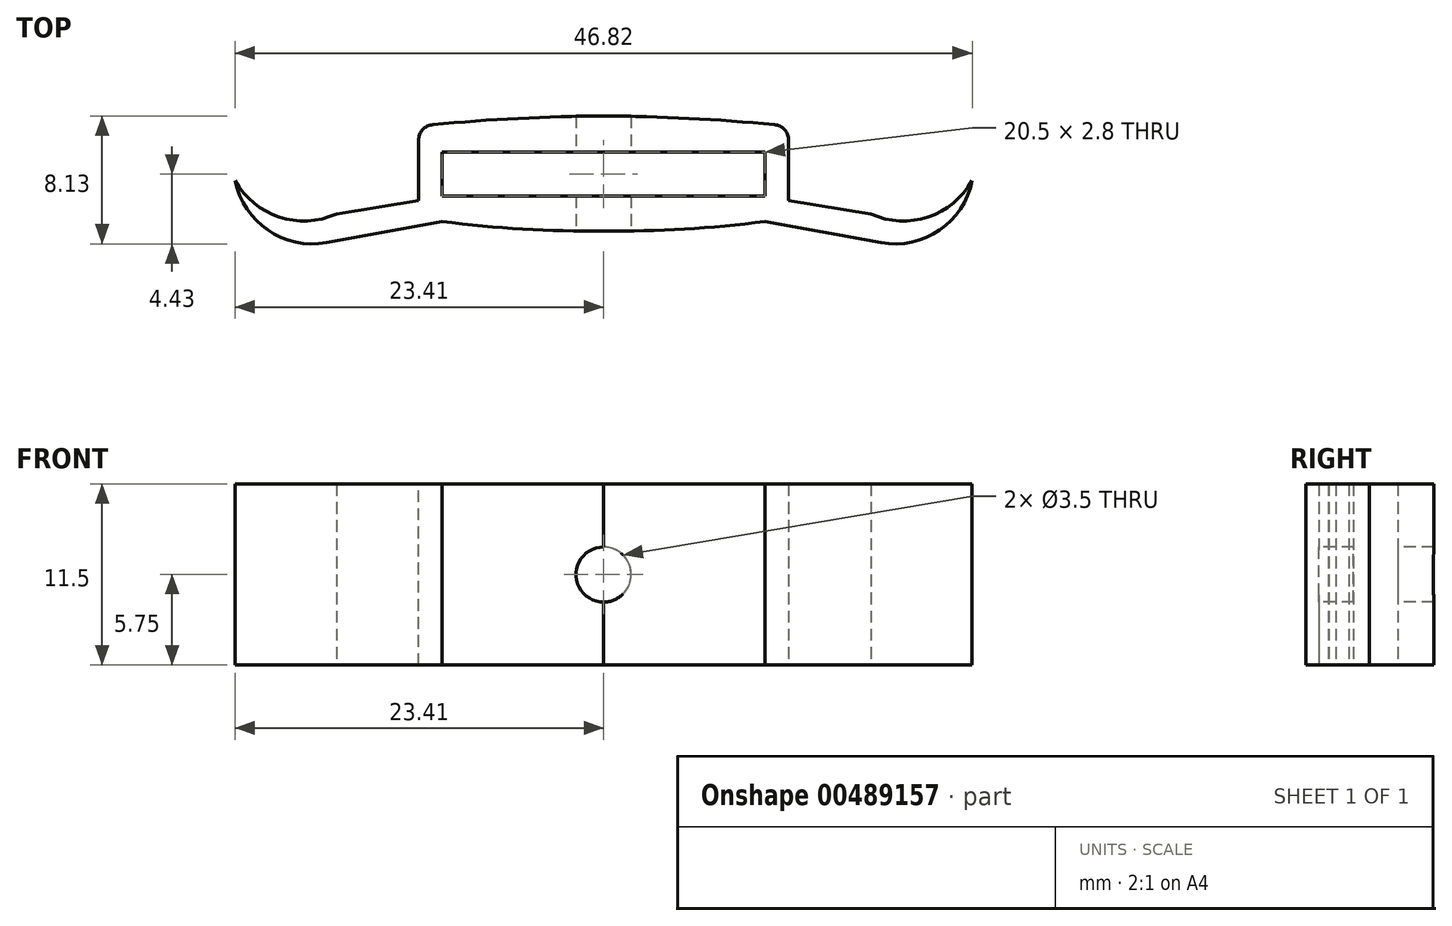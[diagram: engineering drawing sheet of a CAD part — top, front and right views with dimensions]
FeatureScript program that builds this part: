
annotation { "Feature Type Name" : "Feature", "Feature Type Description" : "" }
export const myFeature = defineFeature(function(context is Context, id is Id, definition is map)
    precondition{}
    {
        {
            var Q0;
            Q0=qCreatedBy(makeId("Top.planeOp"),FACE);
            var sketch = newSketch(context, id + "F0", { "sketchPlane" : qUnion([Q0])});
            skLineSegment(sketch, "E0", {"start": v(23.5, -4.04) * mm, "end": v(23.5, 3) * mm, "construction": true});
            skLineSegment(sketch, "E1", {"start": v(29.72, 8.1) * mm, "end": v(-41.61, 8.1) * mm, "construction": true});
            skLineSegment(sketch, "E2", {"start": v(30.67, 18.45) * mm, "end": v(-38.25, 18.45) * mm, "construction": true});
            skLineSegment(sketch, "E3", {"start": v(10.25, -6.45) * mm, "end": v(10.25, 31.2) * mm, "construction": true});
            skLineSegment(sketch, "E4", {"start": v(27.36, 1.4) * mm, "end": v(-25.89, 1.4) * mm, "construction": true});
            skLineSegment(sketch, "E5", {"start": v(10.25, 1.4) * mm, "end": v(17.87, 0) * mm});
            skArc(sketch, "E6", {"start": v(0, 0.8) * mm, "mid": v(5.14, 0.9) * mm, "end": v(10.25, 1.4) * mm});
            skArc(sketch, "E7", {"start": v(16.98, 1.87) * mm, "mid": v(20.6, 1.68) * mm, "end": v(23.4, 4) * mm});
            skLineSegment(sketch, "E8.trimOffspring", {"start": v(23.5, 8.1) * mm, "end": v(23.5, 14.66) * mm, "construction": true});
            skArc(sketch, "E9.trimOffspring", {"start": v(17.58, 0.05) * mm, "mid": v(21.3, 0.83) * mm, "end": v(23.4, 4) * mm});
            skPoint(sketch, "E10.center.orphan", {"position": v(19.03, 5.12) * mm});
            skLineSegment(sketch, "E11", {"start": v(10.25, 3) * mm, "end": v(10.25, 5.8) * mm});
            skLineSegment(sketch, "E12", {"start": v(10.25, 5.8) * mm, "end": v(0, 5.8) * mm});
            skLineSegment(sketch, "E13", {"start": v(10.25, 3) * mm, "end": v(0, 3) * mm});
            skLineSegment(sketch, "E14", {"start": v(11.75, 2.71) * mm, "end": v(11.75, 7.46) * mm});
            skArc(sketch, "E15", {"start": v(11.75, 7.46) * mm, "mid": v(5.88, 7.92) * mm, "end": v(0, 8.1) * mm});
            skLineSegment(sketch, "E16", {"start": v(23.4, 4) * mm, "end": v(23.4, 4) * mm});
            skLineSegment(sketch, "E17.MirrorCS", {"start": v(-11.75, 2.71) * mm, "end": v(-11.75, 7.46) * mm});
            skLineSegment(sketch, "E18.MirrorCS", {"start": v(-10.25, 3) * mm, "end": v(0, 3) * mm});
            skArc(sketch, "E19.MirrorCS", {"start": v(-11.75, 7.46) * mm, "mid": v(-5.88, 7.92) * mm, "end": v(0, 8.1) * mm});
            skArc(sketch, "E20.MirrorCS", {"start": v(0, 0.8) * mm, "mid": v(-5.14, 0.9) * mm, "end": v(-10.25, 1.4) * mm});
            skLineSegment(sketch, "E21.MirrorCS", {"start": v(-10.25, 3) * mm, "end": v(-10.25, 5.8) * mm});
            skLineSegment(sketch, "E22.MirrorCS", {"start": v(-10.25, 5.8) * mm, "end": v(0, 5.8) * mm});
            skLineSegment(sketch, "E23", {"start": v(11.75, 2.71) * mm, "end": v(16.98, 1.87) * mm});
            skLineSegment(sketch, "E24.MirrorCS", {"start": v(-11.75, 2.71) * mm, "end": v(-16.98, 1.87) * mm});
            skPoint(sketch, "E25.MirrorP", {"position": v(-19.03, 5.12) * mm});
            skLineSegment(sketch, "E26.MirrorCS", {"start": v(-23.4, 4) * mm, "end": v(-23.4, 4) * mm});
            skLineSegment(sketch, "E27.MirrorCS", {"start": v(-10.25, 1.4) * mm, "end": v(-17.87, 0) * mm});
            skLineSegment(sketch, "E28.MirrorCS", {"start": v(-23.5, -4.04) * mm, "end": v(-23.5, 3) * mm, "construction": true});
            skArc(sketch, "E29.MirrorCS", {"start": v(-16.98, 1.87) * mm, "mid": v(-20.6, 1.68) * mm, "end": v(-23.4, 4) * mm});
            skArc(sketch, "E30.MirrorCS", {"start": v(-17.58, 0.05) * mm, "mid": v(-21.3, 0.83) * mm, "end": v(-23.4, 4) * mm});
            skLineSegment(sketch, "E31.MirrorCS", {"start": v(-27.36, 1.4) * mm, "end": v(25.89, 1.4) * mm, "construction": true});
            skSolve(sketch);
        }
        {
            var Q0;
            Q0 = qSketchRegion(id + "F0", true);
            extrude(context, id + "F1", {"entities" : qUnion([Q0]), "depth" : 11.5 * mm});
        }
        {
            var Q0;
            Q0=qCreatedBy(makeId("Front.planeOp"),FACE);
            var sketch = newSketch(context, id + "F2", { "sketchPlane" : qUnion([Q0])});
            skCircle(sketch, "E32", {"center": v(0, 5.75) * mm, "radius": 1.75 * mm});
            skSolve(sketch);
        }
        {
            var Q0;
            Q0 = qSketchRegion(id + "F2", true);
            extrude(context, id + "F3", {"entities" : qUnion([Q0]), "operationType" : NewBodyOperationType.REMOVE, "oppositeDirection" : true, "depth" : 25 * mm});
        }
        {
            var Q0;
            Q0=makeQuery(id+"F1.opExtrude","SWEPT_EDGE",EDGE,{"disambiguationData":[OSD([sQuery(id+"F0.wireOp",EDGE,"E17.MirrorCS"),sQuery(id+"F0.wireOp",EDGE,"E19.MirrorCS")])]});
            var Q1;
            Q1=makeQuery(id+"F1.opExtrude","SWEPT_EDGE",EDGE,{"disambiguationData":[OSD([sQuery(id+"F0.wireOp",EDGE,"E14"),sQuery(id+"F0.wireOp",EDGE,"E15")])]});
            fillet(context, id + "F4", {"entities" : qUnion([Q0, Q1]), "radius" : 1 * mm, "tangentPropagation" : true, "allowEdgeOverflow" : false});
        }
    });
